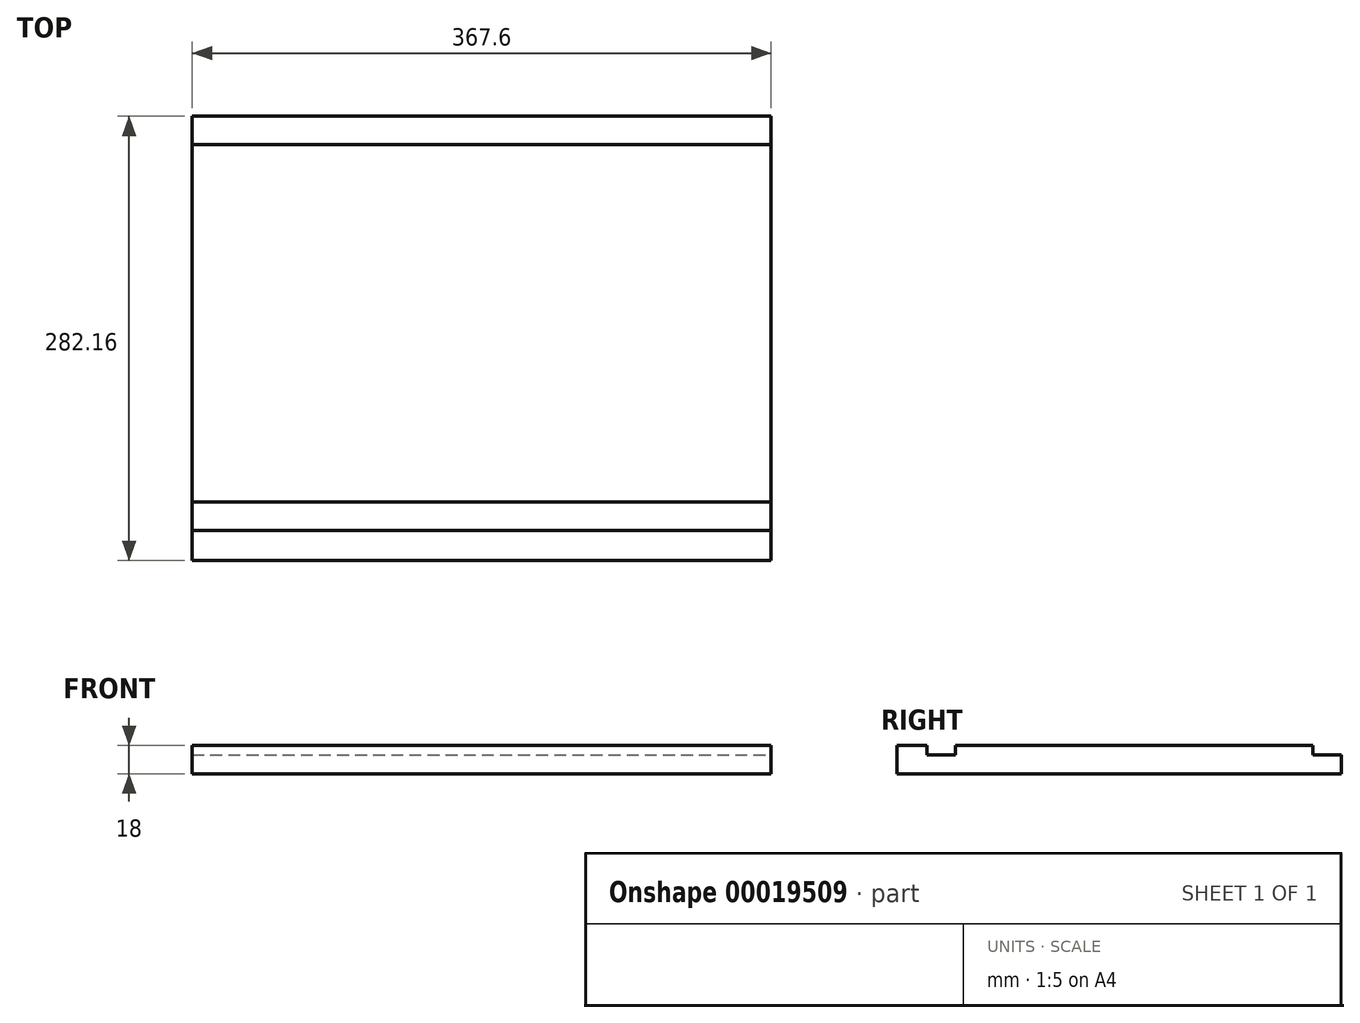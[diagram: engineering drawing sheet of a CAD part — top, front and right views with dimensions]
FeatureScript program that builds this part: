
annotation { "Feature Type Name" : "Feature", "Feature Type Description" : "" }
export const myFeature = defineFeature(function(context is Context, id is Id, definition is map)
    precondition{}
    {
        {
            var Q0;
            Q0=qCreatedBy(makeId("Top.planeOp"),FACE);
            var sketch = newSketch(context, id + "F0", { "sketchPlane" : qUnion([Q0])});
            skLineSegment(sketch, "E0.bottom", {"start": v(-201.28, 124.08) * mm, "end": v(166.32, 124.08) * mm});
            skLineSegment(sketch, "E0.top", {"start": v(-201.28, -158.08) * mm, "end": v(166.32, -158.08) * mm});
            skLineSegment(sketch, "E0.left", {"start": v(-201.28, 124.08) * mm, "end": v(-201.28, -158.08) * mm});
            skLineSegment(sketch, "E0.right", {"start": v(166.32, 124.08) * mm, "end": v(166.32, -158.08) * mm});
            skSolve(sketch);
        }
        {
            var Q0;
            Q0 = qSketchRegion(id + "F0", true);
            extrude(context, id + "F1", {"entities" : qUnion([Q0]), "depth" : 18 * mm});
        }
        {
            var Q0;
            Q0=makeQuery(id+"F1.opExtrude","CAP_FACE",FACE,{"disambiguationData":[OSD([sQuery(id+"F0.wireOp",EDGE,"E0.bottom"),sQuery(id+"F0.wireOp",EDGE,"E0.top"),sQuery(id+"F0.wireOp",EDGE,"E0.left"),sQuery(id+"F0.wireOp",EDGE,"E0.right")])],"isStart":false});
            var sketch = newSketch(context, id + "F2", { "sketchPlane" : qUnion([Q0])});
            skLineSegment(sketch, "E1.bottom", {"start": v(-201.28, -121.03) * mm, "end": v(166.32, -121.03) * mm});
            skLineSegment(sketch, "E1.top", {"start": v(-201.28, -139.03) * mm, "end": v(166.32, -139.03) * mm});
            skLineSegment(sketch, "E1.left", {"start": v(-201.28, -121.03) * mm, "end": v(-201.28, -139.03) * mm});
            skLineSegment(sketch, "E1.right", {"start": v(166.32, -121.03) * mm, "end": v(166.32, -139.03) * mm});
            skSolve(sketch);
        }
        {
            var Q0;
            Q0 = qSketchRegion(id + "F2", true);
            extrude(context, id + "F3", {"entities" : qUnion([Q0]), "operationType" : NewBodyOperationType.REMOVE, "oppositeDirection" : true, "depth" : 6 * mm});
        }
        {
            var Q0;
            {var subQ0=sQuery(id+"F0.wireOp",EDGE,"E0.bottom");var subQ1=sQuery(id+"F0.wireOp",EDGE,"E0.left");var subQ2=sQuery(id+"F0.wireOp",EDGE,"E0.right");Q0=makeQuery(id+"F3.boolean.opBoolean","SPLIT",FACE,{"disambiguationData":[TD([makeQuery(id+"F1.opExtrude","SWEPT_FACE",FACE,{"disambiguationData":[OSD([subQ0])]})])],"derivedFrom":makeQuery(id+"F1.opExtrude","CAP_FACE",FACE,{"disambiguationData":[OSD([subQ0,sQuery(id+"F0.wireOp",EDGE,"E0.top"),subQ1,subQ2])],"isStart":false})});}
            var sketch = newSketch(context, id + "F4", { "sketchPlane" : qUnion([Q0])});
            skLineSegment(sketch, "E2.bottom", {"start": v(-201.28, 124.08) * mm, "end": v(166.32, 124.08) * mm});
            skLineSegment(sketch, "E2.top", {"start": v(-201.28, 106.08) * mm, "end": v(166.32, 106.08) * mm});
            skLineSegment(sketch, "E2.left", {"start": v(-201.28, 124.08) * mm, "end": v(-201.28, 106.08) * mm});
            skLineSegment(sketch, "E2.right", {"start": v(166.32, 124.08) * mm, "end": v(166.32, 106.08) * mm});
            skSolve(sketch);
        }
        {
            var Q0;
            Q0 = qSketchRegion(id + "F4", true);
            extrude(context, id + "F5", {"entities" : qUnion([Q0]), "operationType" : NewBodyOperationType.REMOVE, "oppositeDirection" : true, "depth" : 6 * mm});
        }
    });
